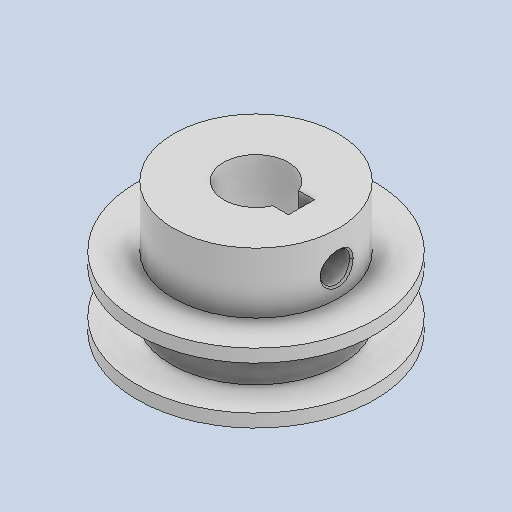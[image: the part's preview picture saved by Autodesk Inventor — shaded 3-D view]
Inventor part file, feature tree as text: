
AUTODESK INVENTOR PART (.ipt)
format: ipt  version: 2024 (Build 280153000, 153)  size: 199,680 bytes
history: native  units: in
note: dims shown in document units (in); Inventor stores cm internally (conversion verified against a paired STEP export)
features: chamfer x1
ambient origin geometry x8: Origin, YZ Plane, XZ Plane, XY Plane, X Axis, Y Axis, Z Axis, Center Point
bodies: Solid1 (feature_tree)
feature tree (1):
  chamfer  "Chamfer1"  [1 undecoded]
note: 1 required parameter value undecoded (feature->parameter linkage not recoverable at this tier; creation-order binding heuristic only, values carry confidence <= 0.55)
